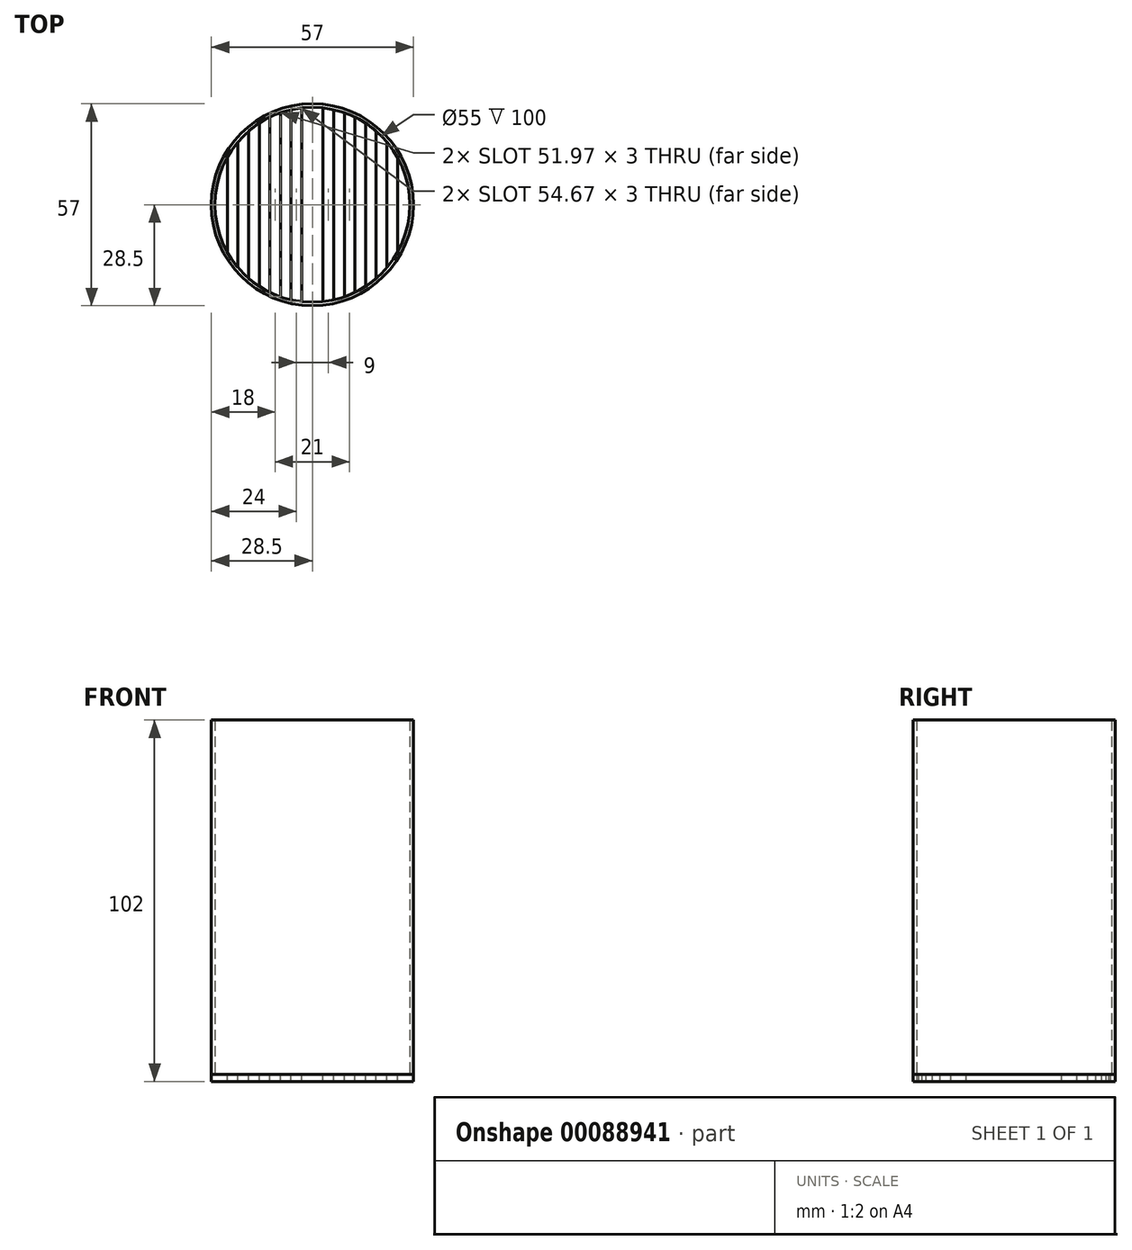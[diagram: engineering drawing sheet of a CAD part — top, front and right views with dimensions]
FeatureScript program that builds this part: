
annotation { "Feature Type Name" : "Feature", "Feature Type Description" : "" }
export const myFeature = defineFeature(function(context is Context, id is Id, definition is map)
    precondition{}
    {
        {
            var Q0;
            Q0=qCreatedBy(makeId("Top.planeOp"),FACE);
            var sketch = newSketch(context, id + "F0", { "sketchPlane" : qUnion([Q0])});
            skCircle(sketch, "E0", {"center": v(0, 0) * mm, "radius": 27.5 * mm});
            skCircle(sketch, "E1", {"center": v(0, 0) * mm, "radius": 28.5 * mm});
            skLineSegment(sketch, "E2", {"start": v(0, 27.5) * mm, "end": v(-7.48, 27.5) * mm});
            skLineSegment(sketch, "E3", {"start": v(0, 27.5) * mm, "end": v(7.48, 27.5) * mm});
            skLineSegment(sketch, "E4.bottom", {"start": v(-7.48, 27.5) * mm, "end": v(-7.48, 27.5) * mm});
            skLineSegment(sketch, "E4.top", {"start": v(-7.48, 31.5) * mm, "end": v(-7.48, 31.5) * mm});
            skLineSegment(sketch, "E4.left", {"start": v(-7.48, 27.5) * mm, "end": v(-7.48, 31.5) * mm});
            skLineSegment(sketch, "E4.right", {"start": v(-7.48, 27.5) * mm, "end": v(-7.48, 31.5) * mm});
            skLineSegment(sketch, "E5", {"start": v(-7.48, 31.5) * mm, "end": v(7.48, 31.5) * mm});
            skLineSegment(sketch, "E6", {"start": v(7.48, 31.5) * mm, "end": v(7.48, 27.5) * mm});
            skSolve(sketch);
        }
        {
            var Q0;
            Q0=makeQuery(id+"F0.imprint","IMPRINT",FACE,{"disambiguationData":[TD([[makeQuery(id+"F0.imprint","IMPRINT",EDGE,{"derivedFrom":sQuery(id+"F0.wireOp",EDGE,"E0")}),1.0]])]});
            var Q1;
            Q1=makeQuery(id+"F0.imprint","IMPRINT",FACE,{"disambiguationData":[TD([[makeQuery(id+"F0.imprint","IMPRINT",EDGE,{"derivedFrom":sQuery(id+"F0.wireOp",EDGE,"E0")}),-1.0]])]});
            var Q2;
            {var subQ0=sQuery(id+"F0.wireOp",EDGE,"E4.right");Q2=makeQuery(id+"F0.imprint","IMPRINT",FACE,{"disambiguationData":[TD([[makeQuery(id+"F0.imprint","IMPRINT",EDGE,{"derivedFrom":subQ0}),-1.0]])]});}
            var Q3;
            {var subQ0=sQuery(id+"F0.wireOp",EDGE,"E2");Q3=makeQuery(id+"F0.imprint","IMPRINT",FACE,{"disambiguationData":[TD([[makeQuery(id+"F0.imprint","IMPRINT",EDGE,{"derivedFrom":subQ0}),-1.0]])]});}
            extrude(context, id + "F1", {"entities" : qUnion([Q0, Q1, Q2, Q3]), "oppositeDirection" : true, "depth" : 2 * mm});
        }
        {
            var Q0;
            Q0=makeQuery(id+"F0.imprint","IMPRINT",FACE,{"disambiguationData":[TD([[makeQuery(id+"F0.imprint","IMPRINT",EDGE,{"derivedFrom":sQuery(id+"F0.wireOp",EDGE,"E0")}),-1.0]])]});
            var Q1;
            {var subQ0=sQuery(id+"F0.wireOp",EDGE,"E2");Q1=makeQuery(id+"F0.imprint","IMPRINT",FACE,{"disambiguationData":[TD([[makeQuery(id+"F0.imprint","IMPRINT",EDGE,{"derivedFrom":subQ0}),-1.0]])]});}
            var Q2;
            {var subQ0=sQuery(id+"F0.wireOp",EDGE,"E4.right");Q2=makeQuery(id+"F0.imprint","IMPRINT",FACE,{"disambiguationData":[TD([[makeQuery(id+"F0.imprint","IMPRINT",EDGE,{"derivedFrom":subQ0}),-1.0]])]});}
            extrude(context, id + "F2", {"entities" : qUnion([Q0, Q1, Q2]), "depth" : 100 * mm});
        }
        {
            var Q0;
            Q0=qCreatedBy(makeId("Top.planeOp"),FACE);
            var sketch = newSketch(context, id + "F3", { "sketchPlane" : qUnion([Q0])});
            skCircle(sketch, "E7", {"center": v(0, 0) * mm, "radius": 27.5 * mm});
            skLineSegment(sketch, "E8", {"start": v(0, 0) * mm, "end": v(-3, 0) * mm});
            skLineSegment(sketch, "E9", {"start": v(-3, 0) * mm, "end": v(-6, 0) * mm});
            skLineSegment(sketch, "E10", {"start": v(-6, 0) * mm, "end": v(-9, 0) * mm});
            skLineSegment(sketch, "E11", {"start": v(-9, 0) * mm, "end": v(-12, 0) * mm});
            skLineSegment(sketch, "E12", {"start": v(-12, 0) * mm, "end": v(-15, 0) * mm});
            skLineSegment(sketch, "E13", {"start": v(-15, 0) * mm, "end": v(-18, 0) * mm});
            skLineSegment(sketch, "E14", {"start": v(-18, 0) * mm, "end": v(-21, 0) * mm});
            skLineSegment(sketch, "E15", {"start": v(-21, 0) * mm, "end": v(-24, 0) * mm});
            skLineSegment(sketch, "E16", {"start": v(-24, 0) * mm, "end": v(-27.5, 0) * mm});
            skLineSegment(sketch, "E17", {"start": v(0, 0) * mm, "end": v(3, 0) * mm});
            skLineSegment(sketch, "E18", {"start": v(3, 0) * mm, "end": v(6, 0) * mm});
            skLineSegment(sketch, "E19", {"start": v(6, 0) * mm, "end": v(9, 0) * mm});
            skLineSegment(sketch, "E20", {"start": v(9, 0) * mm, "end": v(12, 0) * mm});
            skLineSegment(sketch, "E21", {"start": v(12, 0) * mm, "end": v(15, 0) * mm});
            skLineSegment(sketch, "E22", {"start": v(15, 0) * mm, "end": v(18, 0) * mm});
            skLineSegment(sketch, "E23", {"start": v(18, 0) * mm, "end": v(21, 0) * mm});
            skLineSegment(sketch, "E24", {"start": v(21, 0) * mm, "end": v(24, 0) * mm});
            skLineSegment(sketch, "E25", {"start": v(24, 0) * mm, "end": v(27.5, 0) * mm});
            skLineSegment(sketch, "E26", {"start": v(-24, 0) * mm, "end": v(-24, 13.43) * mm});
            skLineSegment(sketch, "E27", {"start": v(-24, 0) * mm, "end": v(-24, -13.43) * mm});
            skLineSegment(sketch, "E28", {"start": v(-21, 0) * mm, "end": v(-21, -17.76) * mm});
            skLineSegment(sketch, "E29", {"start": v(-21, -17.76) * mm, "end": v(-21, 17.76) * mm});
            skLineSegment(sketch, "E30", {"start": v(-18, 0) * mm, "end": v(-18, 20.8) * mm});
            skLineSegment(sketch, "E31", {"start": v(-18, 20.8) * mm, "end": v(-18, -20.8) * mm});
            skLineSegment(sketch, "E32", {"start": v(-15, 0) * mm, "end": v(-15, -23.05) * mm});
            skLineSegment(sketch, "E33", {"start": v(-15, -23.05) * mm, "end": v(-15, 23.05) * mm});
            skLineSegment(sketch, "E34", {"start": v(-12, 0) * mm, "end": v(-12, 24.74) * mm});
            skLineSegment(sketch, "E35", {"start": v(-12, 24.74) * mm, "end": v(-12, -24.74) * mm});
            skLineSegment(sketch, "E36", {"start": v(-9, 0) * mm, "end": v(-9, 25.99) * mm});
            skLineSegment(sketch, "E37", {"start": v(-9, 25.99) * mm, "end": v(-9, -25.99) * mm});
            skLineSegment(sketch, "E38", {"start": v(-6, 0) * mm, "end": v(-6, 26.84) * mm});
            skLineSegment(sketch, "E39", {"start": v(-6, 26.84) * mm, "end": v(-6, -26.84) * mm});
            skLineSegment(sketch, "E40", {"start": v(-3, 0) * mm, "end": v(-3, 27.34) * mm});
            skLineSegment(sketch, "E41", {"start": v(-3, 27.34) * mm, "end": v(-3, -27.34) * mm});
            skLineSegment(sketch, "E42", {"start": v(3, 0) * mm, "end": v(3, 27.34) * mm});
            skLineSegment(sketch, "E43", {"start": v(3, 27.34) * mm, "end": v(3, -27.34) * mm});
            skLineSegment(sketch, "E44", {"start": v(6, 0) * mm, "end": v(6, -26.84) * mm});
            skLineSegment(sketch, "E45", {"start": v(6, -26.84) * mm, "end": v(6, 26.84) * mm});
            skLineSegment(sketch, "E46", {"start": v(9, 0) * mm, "end": v(9, 25.99) * mm});
            skLineSegment(sketch, "E47", {"start": v(9, 25.99) * mm, "end": v(9, -25.99) * mm});
            skLineSegment(sketch, "E48", {"start": v(12, 0) * mm, "end": v(12, 24.74) * mm});
            skLineSegment(sketch, "E49", {"start": v(12, 24.74) * mm, "end": v(12, -24.74) * mm});
            skLineSegment(sketch, "E50", {"start": v(15, 0) * mm, "end": v(15, 23.05) * mm});
            skLineSegment(sketch, "E51", {"start": v(15, 23.05) * mm, "end": v(15, -23.05) * mm});
            skLineSegment(sketch, "E52", {"start": v(18, 0) * mm, "end": v(18, 20.8) * mm});
            skLineSegment(sketch, "E53", {"start": v(18, 20.8) * mm, "end": v(18, -20.8) * mm});
            skLineSegment(sketch, "E54", {"start": v(21, 0) * mm, "end": v(21, 17.76) * mm});
            skLineSegment(sketch, "E55", {"start": v(21, 17.76) * mm, "end": v(21, -17.76) * mm});
            skLineSegment(sketch, "E56", {"start": v(24, 0) * mm, "end": v(24, 13.43) * mm});
            skLineSegment(sketch, "E57", {"start": v(24, 13.43) * mm, "end": v(24, -13.43) * mm});
            skSolve(sketch);
        }
        {
            var Q0;
            {var subQ5=sQuery(id+"F3.wireOp",EDGE,"E9");Q0=makeQuery(id+"F3.imprint","IMPRINT",FACE,{"disambiguationData":[TD([[makeQuery(id+"F3.imprint","IMPRINT",EDGE,{"derivedFrom":subQ5}),-1.0]])]});}
            var Q1;
            {var subQ5=sQuery(id+"F3.wireOp",EDGE,"E9");Q1=makeQuery(id+"F3.imprint","IMPRINT",FACE,{"disambiguationData":[TD([[makeQuery(id+"F3.imprint","IMPRINT",EDGE,{"derivedFrom":subQ5}),1.0]])]});}
            var Q2;
            {var subQ5=sQuery(id+"F3.wireOp",EDGE,"E11");Q2=makeQuery(id+"F3.imprint","IMPRINT",FACE,{"disambiguationData":[TD([[makeQuery(id+"F3.imprint","IMPRINT",EDGE,{"derivedFrom":subQ5}),1.0]])]});}
            var Q3;
            {var subQ5=sQuery(id+"F3.wireOp",EDGE,"E11");Q3=makeQuery(id+"F3.imprint","IMPRINT",FACE,{"disambiguationData":[TD([[makeQuery(id+"F3.imprint","IMPRINT",EDGE,{"derivedFrom":subQ5}),-1.0]])]});}
            var Q4;
            {var subQ5=sQuery(id+"F3.wireOp",EDGE,"E13");Q4=makeQuery(id+"F3.imprint","IMPRINT",FACE,{"disambiguationData":[TD([[makeQuery(id+"F3.imprint","IMPRINT",EDGE,{"derivedFrom":subQ5}),-1.0]])]});}
            var Q5;
            {var subQ5=sQuery(id+"F3.wireOp",EDGE,"E13");Q5=makeQuery(id+"F3.imprint","IMPRINT",FACE,{"disambiguationData":[TD([[makeQuery(id+"F3.imprint","IMPRINT",EDGE,{"derivedFrom":subQ5}),1.0]])]});}
            var Q6;
            {var subQ4=sQuery(id+"F3.wireOp",EDGE,"E15");Q6=makeQuery(id+"F3.imprint","IMPRINT",FACE,{"disambiguationData":[TD([[makeQuery(id+"F3.imprint","IMPRINT",EDGE,{"derivedFrom":subQ4}),1.0]])]});}
            var Q7;
            {var subQ4=sQuery(id+"F3.wireOp",EDGE,"E15");Q7=makeQuery(id+"F3.imprint","IMPRINT",FACE,{"disambiguationData":[TD([[makeQuery(id+"F3.imprint","IMPRINT",EDGE,{"derivedFrom":subQ4}),-1.0]])]});}
            var Q8;
            {var subQ5=sQuery(id+"F3.wireOp",EDGE,"E18");Q8=makeQuery(id+"F3.imprint","IMPRINT",FACE,{"disambiguationData":[TD([[makeQuery(id+"F3.imprint","IMPRINT",EDGE,{"derivedFrom":subQ5}),1.0]])]});}
            var Q9;
            {var subQ5=sQuery(id+"F3.wireOp",EDGE,"E18");Q9=makeQuery(id+"F3.imprint","IMPRINT",FACE,{"disambiguationData":[TD([[makeQuery(id+"F3.imprint","IMPRINT",EDGE,{"derivedFrom":subQ5}),-1.0]])]});}
            var Q10;
            {var subQ5=sQuery(id+"F3.wireOp",EDGE,"E20");Q10=makeQuery(id+"F3.imprint","IMPRINT",FACE,{"disambiguationData":[TD([[makeQuery(id+"F3.imprint","IMPRINT",EDGE,{"derivedFrom":subQ5}),-1.0]])]});}
            var Q11;
            {var subQ5=sQuery(id+"F3.wireOp",EDGE,"E20");Q11=makeQuery(id+"F3.imprint","IMPRINT",FACE,{"disambiguationData":[TD([[makeQuery(id+"F3.imprint","IMPRINT",EDGE,{"derivedFrom":subQ5}),1.0]])]});}
            var Q12;
            {var subQ5=sQuery(id+"F3.wireOp",EDGE,"E22");Q12=makeQuery(id+"F3.imprint","IMPRINT",FACE,{"disambiguationData":[TD([[makeQuery(id+"F3.imprint","IMPRINT",EDGE,{"derivedFrom":subQ5}),1.0]])]});}
            var Q13;
            {var subQ5=sQuery(id+"F3.wireOp",EDGE,"E22");Q13=makeQuery(id+"F3.imprint","IMPRINT",FACE,{"disambiguationData":[TD([[makeQuery(id+"F3.imprint","IMPRINT",EDGE,{"derivedFrom":subQ5}),-1.0]])]});}
            var Q14;
            {var subQ5=sQuery(id+"F3.wireOp",EDGE,"E24");Q14=makeQuery(id+"F3.imprint","IMPRINT",FACE,{"disambiguationData":[TD([[makeQuery(id+"F3.imprint","IMPRINT",EDGE,{"derivedFrom":subQ5}),1.0]])]});}
            var Q15;
            {var subQ5=sQuery(id+"F3.wireOp",EDGE,"E24");Q15=makeQuery(id+"F3.imprint","IMPRINT",FACE,{"disambiguationData":[TD([[makeQuery(id+"F3.imprint","IMPRINT",EDGE,{"derivedFrom":subQ5}),-1.0]])]});}
            extrude(context, id + "F4", {"entities" : qUnion([Q0, Q1, Q2, Q3, Q4, Q5, Q6, Q7, Q8, Q9, Q10, Q11, Q12, Q13, Q14, Q15]), "operationType" : NewBodyOperationType.REMOVE, "oppositeDirection" : true, "depth" : 2 * mm});
        }
    });
